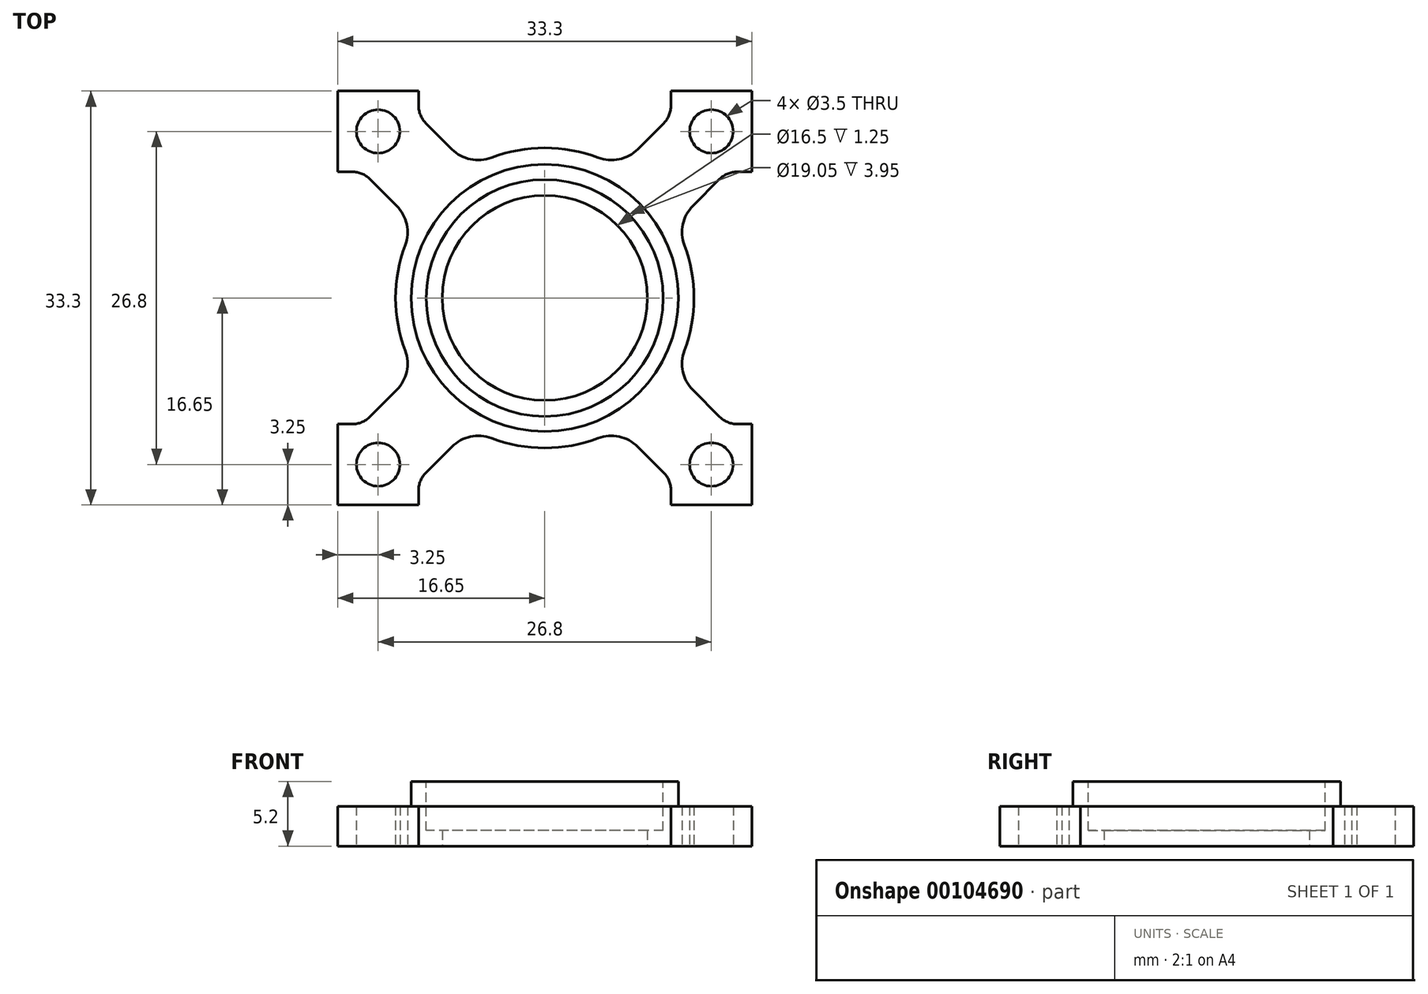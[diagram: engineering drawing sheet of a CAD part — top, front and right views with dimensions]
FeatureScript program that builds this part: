
annotation { "Feature Type Name" : "Feature", "Feature Type Description" : "" }
export const myFeature = defineFeature(function(context is Context, id is Id, definition is map)
    precondition{}
    {
        {
            var Q0;
            Q0=qCreatedBy(makeId("Top.planeOp"),FACE);
            var sketch = newSketch(context, id + "F0", { "sketchPlane" : qUnion([Q0])});
            skPoint(sketch, "E0.middle", {"position": v(0, 0) * mm});
            skCircle(sketch, "E1", {"center": v(0, 0) * mm, "radius": 8.25 * mm});
            skArc(sketch, "E2", {"start": v(10.43, -5.93) * mm, "mid": v(12, 0) * mm, "end": v(10.43, 5.93) * mm});
            skLineSegment(sketch, "E3.MirrorCS", {"start": v(-16.65, -16.65) * mm, "end": v(-10.15, -16.65) * mm});
            skLineSegment(sketch, "E4.trimOffspring", {"start": v(-10.15, -16.65) * mm, "end": v(-16.65, -16.65) * mm});
            skLineSegment(sketch, "E5", {"start": v(10.15, 16.65) * mm, "end": v(16.65, 16.65) * mm});
            skLineSegment(sketch, "E6", {"start": v(16.65, 10.15) * mm, "end": v(16.65, 16.65) * mm});
            skLineSegment(sketch, "E7", {"start": v(16.65, -10.15) * mm, "end": v(16.65, -16.65) * mm});
            skLineSegment(sketch, "E8", {"start": v(10.15, -16.65) * mm, "end": v(16.65, -16.65) * mm});
            skLineSegment(sketch, "E9", {"start": v(-16.65, -10.15) * mm, "end": v(-16.65, -16.65) * mm});
            skLineSegment(sketch, "E10", {"start": v(-16.65, 16.65) * mm, "end": v(-10.15, 16.65) * mm});
            skLineSegment(sketch, "E11", {"start": v(-16.65, 16.65) * mm, "end": v(-16.65, 10.15) * mm});
            skLineSegment(sketch, "E12", {"start": v(-16.65, 10.15) * mm, "end": v(-14.65, 10.15) * mm});
            skLineSegment(sketch, "E13", {"start": v(-14.65, 10.15) * mm, "end": v(-10.43, 5.93) * mm});
            skLineSegment(sketch, "E14", {"start": v(-10.15, 16.65) * mm, "end": v(-10.15, 14.65) * mm});
            skLineSegment(sketch, "E15", {"start": v(-10.15, 14.65) * mm, "end": v(-5.98, 10.48) * mm});
            skLineSegment(sketch, "E16.MirrorCS", {"start": v(10.15, 14.65) * mm, "end": v(5.98, 10.48) * mm});
            skLineSegment(sketch, "E17.MirrorCS", {"start": v(10.15, 16.65) * mm, "end": v(10.15, 14.65) * mm});
            skLineSegment(sketch, "E18.MirrorCS", {"start": v(14.65, 10.15) * mm, "end": v(10.43, 5.93) * mm});
            skLineSegment(sketch, "E19.MirrorCS", {"start": v(16.65, 10.15) * mm, "end": v(14.65, 10.15) * mm});
            skLineSegment(sketch, "E20.MirrorCS", {"start": v(-14.65, -10.15) * mm, "end": v(-10.43, -5.93) * mm});
            skLineSegment(sketch, "E21.MirrorCS", {"start": v(-16.65, -10.15) * mm, "end": v(-14.65, -10.15) * mm});
            skLineSegment(sketch, "E22.MirrorCS", {"start": v(-10.15, -16.65) * mm, "end": v(-10.15, -14.65) * mm});
            skLineSegment(sketch, "E23.MirrorCS", {"start": v(-10.15, -14.65) * mm, "end": v(-5.98, -10.48) * mm});
            skLineSegment(sketch, "E24.MirrorCS", {"start": v(14.65, -10.15) * mm, "end": v(10.43, -5.93) * mm});
            skLineSegment(sketch, "E25.MirrorCS", {"start": v(16.65, -10.15) * mm, "end": v(14.65, -10.15) * mm});
            skLineSegment(sketch, "E26.MirrorCS", {"start": v(10.15, -16.65) * mm, "end": v(10.15, -14.65) * mm});
            skLineSegment(sketch, "E27.MirrorCS", {"start": v(10.15, -14.65) * mm, "end": v(5.98, -10.48) * mm});
            skArc(sketch, "E28", {"start": v(-5.98, -10.48) * mm, "mid": v(0, -12.07) * mm, "end": v(5.98, -10.48) * mm});
            skArc(sketch, "E29.trimOffspring", {"start": v(-10.43, 5.93) * mm, "mid": v(-12, 0) * mm, "end": v(-10.43, -5.93) * mm});
            skArc(sketch, "E30", {"start": v(-5.98, 10.48) * mm, "mid": v(0, 12.07) * mm, "end": v(5.98, 10.48) * mm});
            skCircle(sketch, "E31", {"center": v(-13.4, 13.4) * mm, "radius": 1.75 * mm});
            skCircle(sketch, "E32.MirrorC", {"center": v(13.4, 13.4) * mm, "radius": 1.75 * mm});
            skCircle(sketch, "E33.MirrorC", {"center": v(13.4, -13.4) * mm, "radius": 1.75 * mm});
            skCircle(sketch, "E34.MirrorC", {"center": v(-13.4, -13.4) * mm, "radius": 1.75 * mm});
            skSolve(sketch);
        }
        {
            var Q0;
            Q0 = qSketchRegion(id + "F0", true);
            extrude(context, id + "F1", {"entities" : qUnion([Q0]), "depth" : 3.2 * mm});
        }
        {
            var Q0;
            Q0=makeQuery(id+"F1.opExtrude","CAP_FACE",FACE,{"disambiguationData":[OSD([sQuery(id+"F0.wireOp",EDGE,"E1"),sQuery(id+"F0.wireOp",EDGE,"E2"),sQuery(id+"F0.wireOp",EDGE,"E4.trimOffspring"),sQuery(id+"F0.wireOp",EDGE,"E5"),sQuery(id+"F0.wireOp",EDGE,"E6"),sQuery(id+"F0.wireOp",EDGE,"E7"),sQuery(id+"F0.wireOp",EDGE,"E8"),sQuery(id+"F0.wireOp",EDGE,"E9"),sQuery(id+"F0.wireOp",EDGE,"E10"),sQuery(id+"F0.wireOp",EDGE,"E11"),sQuery(id+"F0.wireOp",EDGE,"E12"),sQuery(id+"F0.wireOp",EDGE,"E13"),sQuery(id+"F0.wireOp",EDGE,"E14"),sQuery(id+"F0.wireOp",EDGE,"E15"),sQuery(id+"F0.wireOp",EDGE,"E16.MirrorCS"),sQuery(id+"F0.wireOp",EDGE,"E17.MirrorCS"),sQuery(id+"F0.wireOp",EDGE,"E18.MirrorCS"),sQuery(id+"F0.wireOp",EDGE,"E19.MirrorCS"),sQuery(id+"F0.wireOp",EDGE,"E20.MirrorCS"),sQuery(id+"F0.wireOp",EDGE,"E21.MirrorCS"),sQuery(id+"F0.wireOp",EDGE,"E22.MirrorCS"),sQuery(id+"F0.wireOp",EDGE,"E23.MirrorCS"),sQuery(id+"F0.wireOp",EDGE,"E24.MirrorCS"),sQuery(id+"F0.wireOp",EDGE,"E25.MirrorCS"),sQuery(id+"F0.wireOp",EDGE,"E26.MirrorCS"),sQuery(id+"F0.wireOp",EDGE,"E27.MirrorCS"),sQuery(id+"F0.wireOp",EDGE,"E28"),sQuery(id+"F0.wireOp",EDGE,"E29.trimOffspring"),sQuery(id+"F0.wireOp",EDGE,"E30"),sQuery(id+"F0.wireOp",EDGE,"E31"),sQuery(id+"F0.wireOp",EDGE,"E32.MirrorC"),sQuery(id+"F0.wireOp",EDGE,"E33.MirrorC"),sQuery(id+"F0.wireOp",EDGE,"E34.MirrorC")])],"isStart":false});
            var sketch = newSketch(context, id + "F2", { "sketchPlane" : qUnion([Q0])});
            skCircle(sketch, "E35", {"center": v(0, 0) * mm, "radius": 9.53 * mm});
            skSolve(sketch);
        }
        {
            var Q0;
            Q0 = qSketchRegion(id + "F2", true);
            extrude(context, id + "F3", {"entities" : qUnion([Q0]), "operationType" : NewBodyOperationType.REMOVE, "oppositeDirection" : true, "depth" : 1.95 * mm});
        }
        {
            var Q0;
            Q0=makeQuery(id+"F1.opExtrude","CAP_FACE",FACE,{"disambiguationData":[OSD([sQuery(id+"F0.wireOp",EDGE,"E1"),sQuery(id+"F0.wireOp",EDGE,"E2"),sQuery(id+"F0.wireOp",EDGE,"E4.trimOffspring"),sQuery(id+"F0.wireOp",EDGE,"E5"),sQuery(id+"F0.wireOp",EDGE,"E6"),sQuery(id+"F0.wireOp",EDGE,"E7"),sQuery(id+"F0.wireOp",EDGE,"E8"),sQuery(id+"F0.wireOp",EDGE,"E9"),sQuery(id+"F0.wireOp",EDGE,"E10"),sQuery(id+"F0.wireOp",EDGE,"E11"),sQuery(id+"F0.wireOp",EDGE,"E12"),sQuery(id+"F0.wireOp",EDGE,"E13"),sQuery(id+"F0.wireOp",EDGE,"E14"),sQuery(id+"F0.wireOp",EDGE,"E15"),sQuery(id+"F0.wireOp",EDGE,"E16.MirrorCS"),sQuery(id+"F0.wireOp",EDGE,"E17.MirrorCS"),sQuery(id+"F0.wireOp",EDGE,"E18.MirrorCS"),sQuery(id+"F0.wireOp",EDGE,"E19.MirrorCS"),sQuery(id+"F0.wireOp",EDGE,"E20.MirrorCS"),sQuery(id+"F0.wireOp",EDGE,"E21.MirrorCS"),sQuery(id+"F0.wireOp",EDGE,"E22.MirrorCS"),sQuery(id+"F0.wireOp",EDGE,"E23.MirrorCS"),sQuery(id+"F0.wireOp",EDGE,"E24.MirrorCS"),sQuery(id+"F0.wireOp",EDGE,"E25.MirrorCS"),sQuery(id+"F0.wireOp",EDGE,"E26.MirrorCS"),sQuery(id+"F0.wireOp",EDGE,"E27.MirrorCS"),sQuery(id+"F0.wireOp",EDGE,"E28"),sQuery(id+"F0.wireOp",EDGE,"E29.trimOffspring"),sQuery(id+"F0.wireOp",EDGE,"E30"),sQuery(id+"F0.wireOp",EDGE,"E31"),sQuery(id+"F0.wireOp",EDGE,"E32.MirrorC"),sQuery(id+"F0.wireOp",EDGE,"E33.MirrorC"),sQuery(id+"F0.wireOp",EDGE,"E34.MirrorC")])],"isStart":false});
            var sketch = newSketch(context, id + "F4", { "sketchPlane" : qUnion([Q0])});
            skCircle(sketch, "E36", {"center": v(0, 0) * mm, "radius": 10.75 * mm});
            skCircle(sketch, "E37", {"center": v(0, 0) * mm, "radius": 9.53 * mm});
            skSolve(sketch);
        }
        {
            var Q0;
            Q0 = qSketchRegion(id + "F4", true);
            extrude(context, id + "F5", {"entities" : qUnion([Q0]), "operationType" : NewBodyOperationType.ADD, "depth" : 2 * mm});
        }
        {
            var Q0;
            Q0=makeQuery(id+"F1.opExtrude","SWEPT_EDGE",EDGE,{"disambiguationData":[OSD([sQuery(id+"F0.wireOp",EDGE,"E12"),sQuery(id+"F0.wireOp",EDGE,"E13")])]});
            var Q1;
            Q1=makeQuery(id+"F1.opExtrude","SWEPT_EDGE",EDGE,{"disambiguationData":[OSD([sQuery(id+"F0.wireOp",EDGE,"E14"),sQuery(id+"F0.wireOp",EDGE,"E15")])]});
            var Q2;
            Q2=makeQuery(id+"F1.opExtrude","SWEPT_EDGE",EDGE,{"disambiguationData":[OSD([sQuery(id+"F0.wireOp",EDGE,"E16.MirrorCS"),sQuery(id+"F0.wireOp",EDGE,"E17.MirrorCS")])]});
            var Q3;
            Q3=makeQuery(id+"F1.opExtrude","SWEPT_EDGE",EDGE,{"disambiguationData":[OSD([sQuery(id+"F0.wireOp",EDGE,"E18.MirrorCS"),sQuery(id+"F0.wireOp",EDGE,"E19.MirrorCS")])]});
            var Q4;
            Q4=makeQuery(id+"F1.opExtrude","SWEPT_EDGE",EDGE,{"disambiguationData":[OSD([sQuery(id+"F0.wireOp",EDGE,"E24.MirrorCS"),sQuery(id+"F0.wireOp",EDGE,"E25.MirrorCS")])]});
            var Q5;
            Q5=makeQuery(id+"F1.opExtrude","SWEPT_EDGE",EDGE,{"disambiguationData":[OSD([sQuery(id+"F0.wireOp",EDGE,"E26.MirrorCS"),sQuery(id+"F0.wireOp",EDGE,"E27.MirrorCS")])]});
            var Q6;
            Q6=makeQuery(id+"F1.opExtrude","SWEPT_EDGE",EDGE,{"disambiguationData":[OSD([sQuery(id+"F0.wireOp",EDGE,"E22.MirrorCS"),sQuery(id+"F0.wireOp",EDGE,"E23.MirrorCS")])]});
            var Q7;
            Q7=makeQuery(id+"F1.opExtrude","SWEPT_EDGE",EDGE,{"disambiguationData":[OSD([sQuery(id+"F0.wireOp",EDGE,"E20.MirrorCS"),sQuery(id+"F0.wireOp",EDGE,"E21.MirrorCS")])]});
            fillet(context, id + "F6", {"entities" : qUnion([Q0, Q1, Q2, Q3, Q4, Q5, Q6, Q7]), "radius" : 2 * mm, "tangentPropagation" : true, "allowEdgeOverflow" : false});
        }
        {
            var Q0;
            Q0=makeQuery(id+"F1.opExtrude","SWEPT_EDGE",EDGE,{"disambiguationData":[OSD([sQuery(id+"F0.wireOp",EDGE,"E20.MirrorCS"),sQuery(id+"F0.wireOp",EDGE,"E29.trimOffspring")])]});
            var Q1;
            Q1=makeQuery(id+"F1.opExtrude","SWEPT_EDGE",EDGE,{"disambiguationData":[OSD([sQuery(id+"F0.wireOp",EDGE,"E13"),sQuery(id+"F0.wireOp",EDGE,"E29.trimOffspring")])]});
            var Q2;
            Q2=makeQuery(id+"F1.opExtrude","SWEPT_EDGE",EDGE,{"disambiguationData":[OSD([sQuery(id+"F0.wireOp",EDGE,"E15"),sQuery(id+"F0.wireOp",EDGE,"E30")])]});
            var Q3;
            Q3=makeQuery(id+"F1.opExtrude","SWEPT_EDGE",EDGE,{"disambiguationData":[OSD([sQuery(id+"F0.wireOp",EDGE,"E16.MirrorCS"),sQuery(id+"F0.wireOp",EDGE,"E30")])]});
            var Q4;
            Q4=makeQuery(id+"F1.opExtrude","SWEPT_EDGE",EDGE,{"disambiguationData":[OSD([sQuery(id+"F0.wireOp",EDGE,"E2"),sQuery(id+"F0.wireOp",EDGE,"E18.MirrorCS")])]});
            var Q5;
            Q5=makeQuery(id+"F1.opExtrude","SWEPT_EDGE",EDGE,{"disambiguationData":[OSD([sQuery(id+"F0.wireOp",EDGE,"E2"),sQuery(id+"F0.wireOp",EDGE,"E24.MirrorCS")])]});
            var Q6;
            Q6=makeQuery(id+"F1.opExtrude","SWEPT_EDGE",EDGE,{"disambiguationData":[OSD([sQuery(id+"F0.wireOp",EDGE,"E23.MirrorCS"),sQuery(id+"F0.wireOp",EDGE,"E28")])]});
            var Q7;
            Q7=makeQuery(id+"F1.opExtrude","SWEPT_EDGE",EDGE,{"disambiguationData":[OSD([sQuery(id+"F0.wireOp",EDGE,"E27.MirrorCS"),sQuery(id+"F0.wireOp",EDGE,"E28")])]});
            fillet(context, id + "F7", {"entities" : qUnion([Q0, Q1, Q2, Q3, Q4, Q5, Q6, Q7]), "radius" : 3 * mm, "tangentPropagation" : true, "allowEdgeOverflow" : false});
        }
    });
